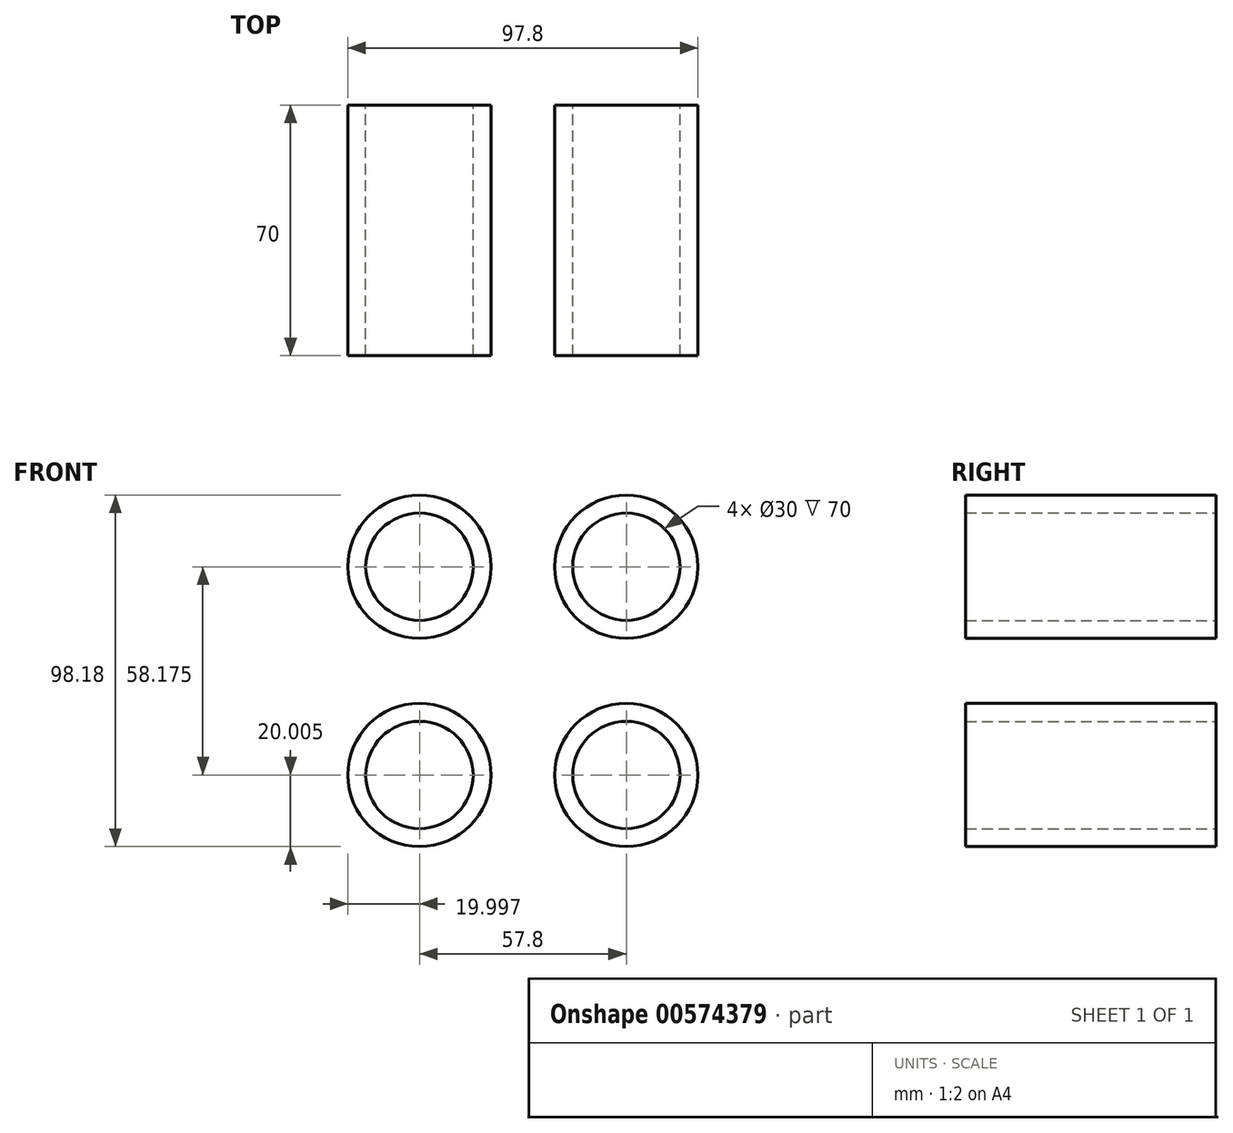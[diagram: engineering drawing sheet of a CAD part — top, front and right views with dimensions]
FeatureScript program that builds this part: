
annotation { "Feature Type Name" : "Feature", "Feature Type Description" : "" }
export const myFeature = defineFeature(function(context is Context, id is Id, definition is map)
    precondition{}
    {
        {
            var Q0;
            Q0=qCreatedBy(makeId("Front.planeOp"),FACE);
            var sketch = newSketch(context, id + "F0", { "sketchPlane" : qUnion([Q0])});
            skLineSegment(sketch, "E0.bottom", {"start": v(-28.21, 28) * mm, "end": v(29.59, 28) * mm, "construction": true});
            skLineSegment(sketch, "E0.top", {"start": v(-28.21, -30.17) * mm, "end": v(29.59, -30.17) * mm, "construction": true});
            skLineSegment(sketch, "E0.left", {"start": v(-28.21, 28) * mm, "end": v(-28.21, -30.17) * mm, "construction": true});
            skLineSegment(sketch, "E0.right", {"start": v(29.59, 28) * mm, "end": v(29.59, -30.17) * mm, "construction": true});
            skCircle(sketch, "E1", {"center": v(-28.21, 28) * mm, "radius": 20 * mm});
            skCircle(sketch, "E2", {"center": v(-28.21, 28) * mm, "radius": 15 * mm});
            skCircle(sketch, "E3", {"center": v(29.59, 28) * mm, "radius": 20 * mm});
            skCircle(sketch, "E4", {"center": v(29.59, 28) * mm, "radius": 15 * mm});
            skCircle(sketch, "E5", {"center": v(-28.21, -30.17) * mm, "radius": 20 * mm});
            skCircle(sketch, "E6", {"center": v(-28.21, -30.17) * mm, "radius": 15 * mm});
            skCircle(sketch, "E7", {"center": v(29.59, -30.17) * mm, "radius": 15 * mm});
            skCircle(sketch, "E8", {"center": v(29.59, -30.17) * mm, "radius": 20 * mm});
            skSolve(sketch);
        }
        {
            var Q0;
            Q0=makeQuery(id+"F0.imprint","IMPRINT",FACE,{"disambiguationData":[TD([[makeQuery(id+"F0.imprint","IMPRINT",EDGE,{"derivedFrom":sQuery(id+"F0.wireOp",EDGE,"E1")}),1.0]])]});
            var Q1;
            Q1=makeQuery(id+"F0.imprint","IMPRINT",FACE,{"disambiguationData":[TD([[makeQuery(id+"F0.imprint","IMPRINT",EDGE,{"derivedFrom":sQuery(id+"F0.wireOp",EDGE,"E3")}),1.0]])]});
            var Q2;
            Q2=makeQuery(id+"F0.imprint","IMPRINT",FACE,{"disambiguationData":[TD([[makeQuery(id+"F0.imprint","IMPRINT",EDGE,{"derivedFrom":sQuery(id+"F0.wireOp",EDGE,"E7")}),-1.0]])]});
            var Q3;
            Q3=makeQuery(id+"F0.imprint","IMPRINT",FACE,{"disambiguationData":[TD([[makeQuery(id+"F0.imprint","IMPRINT",EDGE,{"derivedFrom":sQuery(id+"F0.wireOp",EDGE,"E5")}),1.0]])]});
            extrude(context, id + "F1", {"entities" : qUnion([Q0, Q1, Q2, Q3]), "depth" : 70 * mm, "offsetDistance" : 25 * mm});
        }
    });
